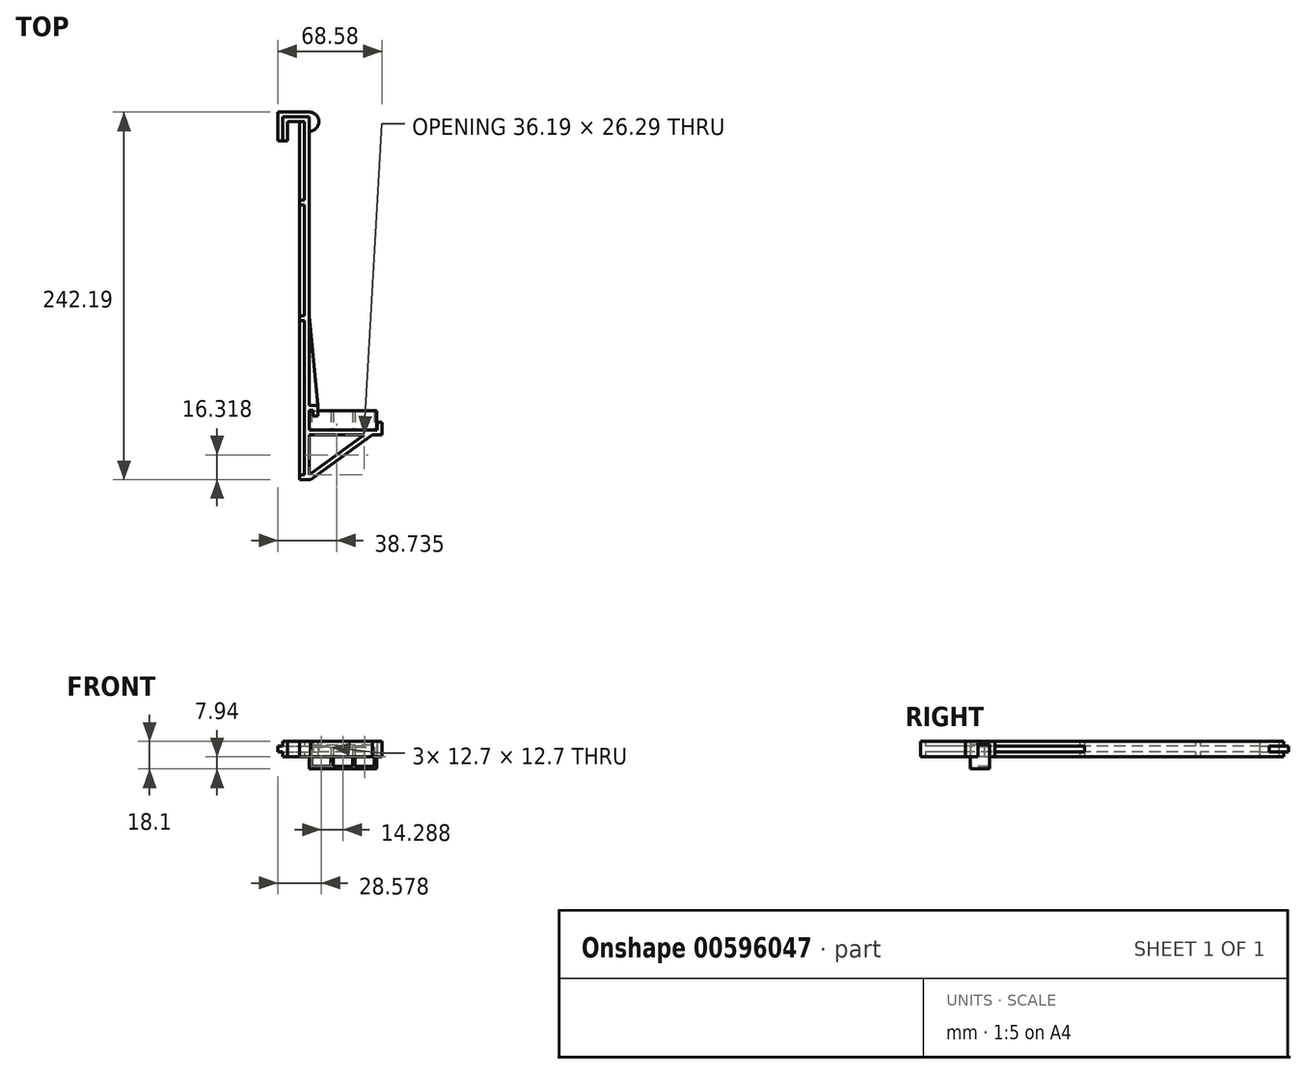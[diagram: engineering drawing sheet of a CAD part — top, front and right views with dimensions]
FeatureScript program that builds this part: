
annotation { "Feature Type Name" : "Feature", "Feature Type Description" : "" }
export const myFeature = defineFeature(function(context is Context, id is Id, definition is map)
    precondition{}
    {
        {
            var Q0;
            Q0=qCreatedBy(makeId("Top.planeOp"),FACE);
            var sketch = newSketch(context, id + "F0", { "sketchPlane" : qUnion([Q0])});
            skLineSegment(sketch, "E0", {"start": v(-17.46, 190.5) * mm, "end": v(-17.46, 206.38) * mm});
            skLineSegment(sketch, "E1", {"start": v(-17.46, 206.38) * mm, "end": v(0, 206.38) * mm});
            skLineSegment(sketch, "E2", {"start": v(0, 206.38) * mm, "end": v(0, 16.2) * mm});
            skLineSegment(sketch, "E3", {"start": v(0, 16.2) * mm, "end": v(5.71, 16.2) * mm});
            skLineSegment(sketch, "E4", {"start": v(5.71, 16.2) * mm, "end": v(5.71, 9.2) * mm});
            skLineSegment(sketch, "E5", {"start": v(5.71, 9.2) * mm, "end": v(2.54, 9.2) * mm});
            skLineSegment(sketch, "E6", {"start": v(2.54, 9.2) * mm, "end": v(2.54, 13.02) * mm});
            skLineSegment(sketch, "E7", {"start": v(2.54, 13.02) * mm, "end": v(0, 13.02) * mm});
            skLineSegment(sketch, "E8", {"start": v(0, 13.02) * mm, "end": v(0, 0) * mm});
            skLineSegment(sketch, "E9", {"start": v(0, 0) * mm, "end": v(44.77, 0) * mm});
            skLineSegment(sketch, "E10", {"start": v(44.77, 0) * mm, "end": v(44.77, 5.08) * mm});
            skLineSegment(sketch, "E11", {"start": v(44.77, 5.08) * mm, "end": v(47.94, 5.08) * mm});
            skLineSegment(sketch, "E12", {"start": v(47.94, 5.08) * mm, "end": v(47.94, -3.17) * mm});
            skLineSegment(sketch, "E13", {"start": v(47.94, -3.17) * mm, "end": v(41.6, -3.17) * mm});
            skLineSegment(sketch, "E14", {"start": v(41.6, -3.17) * mm, "end": v(1.03, -32.64) * mm});
            skLineSegment(sketch, "E15", {"start": v(1.03, -32.64) * mm, "end": v(-6.35, -32.64) * mm});
            skLineSegment(sketch, "E16", {"start": v(-6.35, -32.64) * mm, "end": v(-6.35, -29.47) * mm});
            skLineSegment(sketch, "E17", {"start": v(-6.35, -29.47) * mm, "end": v(-3.17, -29.47) * mm});
            skLineSegment(sketch, "E18", {"start": v(-17.46, 190.5) * mm, "end": v(-14.29, 190.5) * mm});
            skLineSegment(sketch, "E19", {"start": v(-14.29, 190.5) * mm, "end": v(-14.29, 203.2) * mm});
            skLineSegment(sketch, "E20", {"start": v(-14.29, 203.2) * mm, "end": v(-3.18, 203.2) * mm});
            skLineSegment(sketch, "E21", {"start": v(-3.18, 203.2) * mm, "end": v(-3.18, 151.5) * mm});
            skLineSegment(sketch, "E22", {"start": v(0, -3.17) * mm, "end": v(0, -29.47) * mm});
            skLineSegment(sketch, "E23", {"start": v(0, -29.47) * mm, "end": v(36.2, -3.17) * mm});
            skLineSegment(sketch, "E24", {"start": v(36.2, -3.17) * mm, "end": v(0, -3.17) * mm});
            skLineSegment(sketch, "E25", {"start": v(-6.35, -29.47) * mm, "end": v(-6.35, 72.13) * mm});
            skLineSegment(sketch, "E26", {"start": v(-3.18, 75.3) * mm, "end": v(-6.35, 75.3) * mm});
            skLineSegment(sketch, "E27", {"start": v(-6.35, 75.3) * mm, "end": v(-6.35, 72.13) * mm});
            skLineSegment(sketch, "E28", {"start": v(-6.35, 72.13) * mm, "end": v(-3.18, 72.13) * mm});
            skLineSegment(sketch, "E29.trimOffspring", {"start": v(-3.18, 72.13) * mm, "end": v(-3.18, -29.47) * mm});
            skLineSegment(sketch, "E30.trimOffspring", {"start": v(-6.35, 148.33) * mm, "end": v(-6.35, 75.3) * mm});
            skLineSegment(sketch, "E31.0", {"start": v(-20.64, 209.55) * mm, "end": v(0, 209.55) * mm});
            skLineSegment(sketch, "E31.1", {"start": v(-20.64, 190.5) * mm, "end": v(-20.64, 209.55) * mm});
            skLineSegment(sketch, "E32", {"start": v(0, 209.55) * mm, "end": v(0, 206.38) * mm});
            skLineSegment(sketch, "E33", {"start": v(-20.64, 190.5) * mm, "end": v(-17.46, 190.5) * mm});
            skLineSegment(sketch, "E34", {"start": v(5.71, 16.2) * mm, "end": v(0, 75.3) * mm});
            skArc(sketch, "E35", {"start": v(0, 196.85) * mm, "mid": v(6.35, 203.2) * mm, "end": v(0, 209.55) * mm});
            skLineSegment(sketch, "E36", {"start": v(-3.18, 151.5) * mm, "end": v(-6.35, 151.5) * mm});
            skLineSegment(sketch, "E37", {"start": v(-6.35, 151.5) * mm, "end": v(-6.35, 148.33) * mm});
            skLineSegment(sketch, "E38", {"start": v(-6.35, 148.33) * mm, "end": v(-3.18, 148.33) * mm});
            skLineSegment(sketch, "E39.trimOffspring", {"start": v(-6.35, 203.2) * mm, "end": v(-6.35, 151.5) * mm});
            skLineSegment(sketch, "E40.trimOffspring", {"start": v(-3.18, 148.33) * mm, "end": v(-3.18, 75.3) * mm});
            skSolve(sketch);
        }
        {
            var Q0;
            Q0=makeQuery(id+"F0.imprint","IMPRINT",FACE,{"disambiguationData":[TD([[makeQuery(id+"F0.imprint","IMPRINT",EDGE,{"derivedFrom":sQuery(id+"F0.wireOp",EDGE,"E0")}),-1.0]])]});
            extrude(context, id + "F1", {"entities" : qUnion([Q0]), "depth" : 10.16 * mm, "offsetDistance" : 25.4 * mm});
        }
        {
            var Q0;
            Q0=makeQuery(id+"F0.imprint","IMPRINT",FACE,{"disambiguationData":[TD([[makeQuery(id+"F0.imprint","IMPRINT",EDGE,{"derivedFrom":sQuery(id+"F0.wireOp",EDGE,"E0")}),1.0]])]});
            var Q1;
            {var subQ0=sQuery(id+"F0.wireOp",EDGE,"E21");Q1=makeQuery(id+"F0.imprint","IMPRINT",FACE,{"disambiguationData":[TD([[makeQuery(id+"F0.imprint","IMPRINT",EDGE,{"derivedFrom":subQ0}),-1.0]])]});}
            var Q2;
            {var subQ2=sQuery(id+"F0.wireOp",EDGE,"E25");Q2=makeQuery(id+"F0.imprint","IMPRINT",FACE,{"disambiguationData":[TD([[makeQuery(id+"F0.imprint","IMPRINT",EDGE,{"derivedFrom":subQ2}),-1.0]])]});}
            var Q3;
            {var subQ0=sQuery(id+"F0.wireOp",EDGE,"E3");Q3=makeQuery(id+"F0.imprint","IMPRINT",FACE,{"disambiguationData":[TD([[makeQuery(id+"F0.imprint","IMPRINT",EDGE,{"derivedFrom":subQ0}),1.0]])]});}
            var Q4;
            Q4=makeQuery(id+"F0.imprint","IMPRINT",FACE,{"disambiguationData":[TD([[makeQuery(id+"F0.imprint","IMPRINT",EDGE,{"derivedFrom":sQuery(id+"F0.wireOp",EDGE,"E22")}),1.0]])]});
            var Q5;
            {var subQ0=sQuery(id+"F0.wireOp",EDGE,"E32");Q5=makeQuery(id+"F0.imprint","IMPRINT",FACE,{"disambiguationData":[TD([[makeQuery(id+"F0.imprint","IMPRINT",EDGE,{"derivedFrom":subQ0}),1.0]])]});}
            var Q6;
            Q6=makeQuery(id+"F0.imprint","IMPRINT",FACE,{"disambiguationData":[TD([[makeQuery(id+"F0.imprint","IMPRINT",EDGE,{"derivedFrom":sQuery(id+"F0.wireOp",EDGE,"E26")}),-1.0]])]});
            extrude(context, id + "F2", {"entities" : qUnion([Q0, Q1, Q2, Q3, Q4, Q5, Q6]), "operationType" : NewBodyOperationType.ADD, "depth" : 7 * mm, "offsetDistance" : 25.4 * mm, "hasSecondDirection" : true, "secondDirectionOppositeDirection" : false, "secondDirectionDepth" : 3.17 * mm});
        }
        {
            var Q0;
            Q0=makeQuery(id+"F1.opExtrude","SWEPT_FACE",FACE,{"disambiguationData":[OSD([sQuery(id+"F0.wireOp",EDGE,"E9")])]});
            var sketch = newSketch(context, id + "F3", { "sketchPlane" : qUnion([Q0])});
            skLineSegment(sketch, "E41.bottom", {"start": v(0, 7.94) * mm, "end": v(-44.45, 7.94) * mm});
            skLineSegment(sketch, "E41.top", {"start": v(0, -7.94) * mm, "end": v(-44.45, -7.94) * mm});
            skLineSegment(sketch, "E41.left", {"start": v(0, 7.94) * mm, "end": v(0, -7.94) * mm});
            skLineSegment(sketch, "E41.right", {"start": v(-44.45, 7.94) * mm, "end": v(-44.45, -7.94) * mm});
            skLineSegment(sketch, "E42.0", {"start": v(-1.59, 6.35) * mm, "end": v(-1.59, -6.35) * mm});
            skLineSegment(sketch, "E42.1", {"start": v(-1.59, 6.35) * mm, "end": v(-14.29, 6.35) * mm});
            skLineSegment(sketch, "E42.2", {"start": v(-42.86, 6.35) * mm, "end": v(-42.86, -6.35) * mm});
            skLineSegment(sketch, "E42.3", {"start": v(-1.59, -6.35) * mm, "end": v(-14.29, -6.35) * mm});
            skLineSegment(sketch, "E43", {"start": v(-14.29, 6.35) * mm, "end": v(-14.29, -6.35) * mm});
            skLineSegment(sketch, "E44", {"start": v(-15.87, 6.35) * mm, "end": v(-15.87, -6.35) * mm});
            skLineSegment(sketch, "E45", {"start": v(-30.16, 6.35) * mm, "end": v(-30.16, -6.35) * mm});
            skLineSegment(sketch, "E46", {"start": v(-28.57, 6.35) * mm, "end": v(-28.57, -6.35) * mm});
            skLineSegment(sketch, "E47.trimOffspring", {"start": v(-15.87, 6.35) * mm, "end": v(-28.57, 6.35) * mm});
            skLineSegment(sketch, "E48.trimOffspring", {"start": v(-15.87, -6.35) * mm, "end": v(-28.57, -6.35) * mm});
            skLineSegment(sketch, "E49.trimOffspring", {"start": v(-30.16, 6.35) * mm, "end": v(-42.86, 6.35) * mm});
            skLineSegment(sketch, "E50.trimOffspring", {"start": v(-30.16, -6.35) * mm, "end": v(-42.86, -6.35) * mm});
            skSolve(sketch);
        }
        {
            var Q0;
            {var subQ14=sQuery(id+"F3.wireOp",EDGE,"E41.top");Q0=makeQuery(id+"F3.imprint","IMPRINT",FACE,{"disambiguationData":[TD([[makeQuery(id+"F3.imprint","IMPRINT",EDGE,{"derivedFrom":subQ14}),-1.0]])]});}
            var Q1;
            {var subQ0=sQuery(id+"F3.wireOp",EDGE,"E42.1");Q1=makeQuery(id+"F3.imprint","IMPRINT",FACE,{"disambiguationData":[TD([[makeQuery(id+"F3.imprint","IMPRINT",EDGE,{"derivedFrom":subQ0}),-1.0]])]});}
            extrude(context, id + "F4", {"entities" : qUnion([Q0, Q1]), "depth" : 12.7 * mm, "offsetDistance" : 25.4 * mm});
        }
    });
